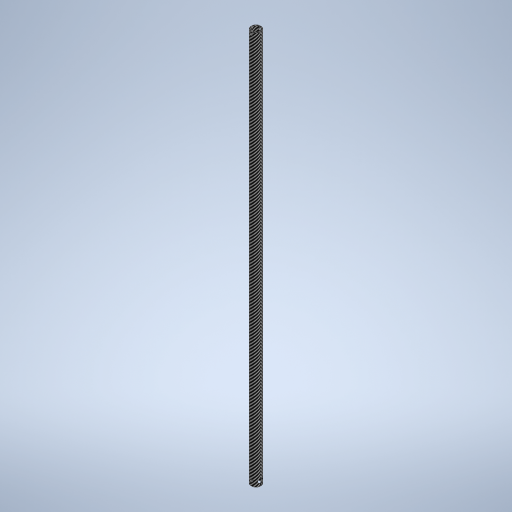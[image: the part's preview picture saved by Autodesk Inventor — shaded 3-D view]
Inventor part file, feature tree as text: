
AUTODESK INVENTOR PART (.ipt)
format: ipt  version: 2023 (Build 270158000, 158)  size: 301,568 bytes
history: native  units: in
note: dims shown in document units (in); Inventor stores cm internally (conversion verified against a paired STEP export)
features: sketch x4, extrude x2, fillet x2, plane x2, hole x2
ambient origin geometry x8: Origin, YZ Plane, XZ Plane, XY Plane, X Axis, Y Axis, Z Axis, Center Point
bodies: Solid1 (feature_tree)
feature tree (12):
  extrude  "Extrusion1"  Depth=0.05in
  fillet  "Fillet1"  Radius=20.0in
  fillet  "Fillet2"  Radius=0.02in
  plane  "Work Plane1"
  extrude  "Extrusion2"  Depth=0.25in
  plane  "Work Plane2"
  hole  "Hole1"  [1 undecoded]
  hole  "Hole2"  [1 undecoded]
  sketch  "Sketch1"  dims[d0=0.5in d1=0.05in d2=20.0in d3=0.0in d4=0.02in]
  sketch  "Sketch2"  dims[d5=0.02in d6=0.25in]
  sketch  "Sketch3"  dims[d7=0.25in d8=0.25in]
  sketch  "Sketch5"  dims[d9=1.0in d10=0.0in d11=0.25in d12=0.25in d13=0.1339in d14=0.75in d15=0.256in d16=0.118in d17=90.0deg d18=1.0in d19=0.8108in d20=0.125in d21=0.1339in d22=0.75in d23=0.375in d24=0.25in d25=0.5635in d26=1.0in d27=0.8108in]
note: 2 required parameter values undecoded (feature->parameter linkage not recoverable at this tier; creation-order binding heuristic only, values carry confidence <= 0.55)
